# Revit family: E-SMART Boiler
name_source: partatom
category: Generic Models
units: mm (PartAtom-declared; Revit-internal decimal feet)

## family parameters
Always vertical = Yes
Can host rebar = No
Cut with Voids When Loaded = No
Host = Wall
Part Type = Normal
Room Calculation Point = No
Round Connector Dimension = Use Diameter
Shared = No

## types (5) — shared parameters
Manufacturer = Masterwatt B.V.
URL = https://masterwatt.nl
Voltage = 230 V
zero-valued in all types: Default Elevation

## per-type parameters (varying)
| type | Art. No. | E-Smart 50 | E-Smart 80 | Model | Watt |
| E-Smart 050 | 200 800 050 | Yes | No | E-Smart boiler 50 Liter | 2000 VA |
| E-Smart 080 | 200 800 080 | No | Yes | E-Smart boiler 80 Liter | 2000 VA |
| E-Smart 100 | 200 800 100 | No | No | E-Smart boiler 100 Liter | 2000 VA |
| E-Smart 120 | 200 800 120 | No | No | E-Smart boiler 120 Liter | 3000 VA |
| E-Smart 150 | 200 800 150 | No | No | E-Smart boiler 150 Liter | 3000 VA |

type visibility flags (boolean, named after types; folded from table):
- E-Smart 050: Yes: (none)
- E-Smart 080: Yes: (none)
- E-Smart 100: Yes: E-Smart 100
- E-Smart 120: Yes: E-Smart 120
- E-Smart 150: Yes: E-Smart 150

## geometry (parser evidence)
native form markers: Sweep x39
no freeform markers — native parametric forms only
